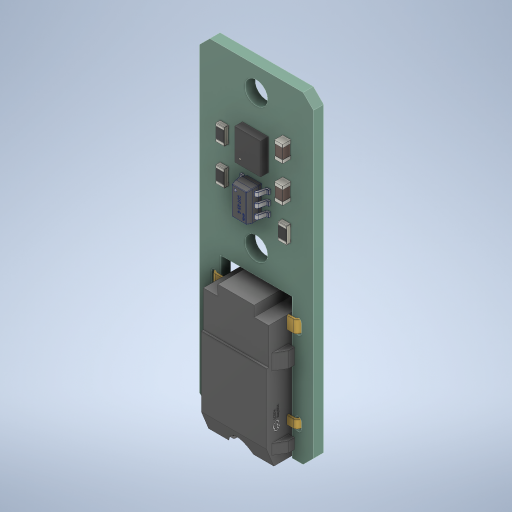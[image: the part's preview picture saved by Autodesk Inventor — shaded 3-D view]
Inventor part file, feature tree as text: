
AUTODESK INVENTOR PART (.ipt)
format: ipt  version: 2024 (Build 280153000, 153)  size: 1,721,344 bytes
history: native  units: in
note: dims shown in document units (in); Inventor stores cm internally (conversion verified against a paired STEP export)
features: move_body x2, direct_edit x1, chamfer x1
ambient origin geometry x8: Origin, YZ Plane, XZ Plane, XY Plane, X Axis, Y Axis, Z Axis, Center Point
bodies: Solid1 (feature_tree), Solid2 (feature_tree), Solid3 (feature_tree), Solid4 (feature_tree), Solid5 (feature_tree), Solid6 (feature_tree), Solid7 (feature_tree), Solid8 (feature_tree), Solid9 (feature_tree), Solid10 (feature_tree), Solid11 (feature_tree), Solid12 (feature_tree), Solid13 (feature_tree), Solid14 (feature_tree), Solid15 (feature_tree), Solid16 (feature_tree), Solid17 (feature_tree), Solid18 (feature_tree), Solid19 (feature_tree), Solid20 (feature_tree), Solid21 (feature_tree), Solid22 (feature_tree), Solid23 (feature_tree), Solid24 (feature_tree), Solid25 (feature_tree), Solid26 (feature_tree), Solid27 (feature_tree), Solid28 (feature_tree)
feature tree (4):
  direct_edit  "Direct Edit1"
  chamfer  "Chamfer1"  Distance=0.001in
  move_body  "Move1"
  move_body  "Move2"
